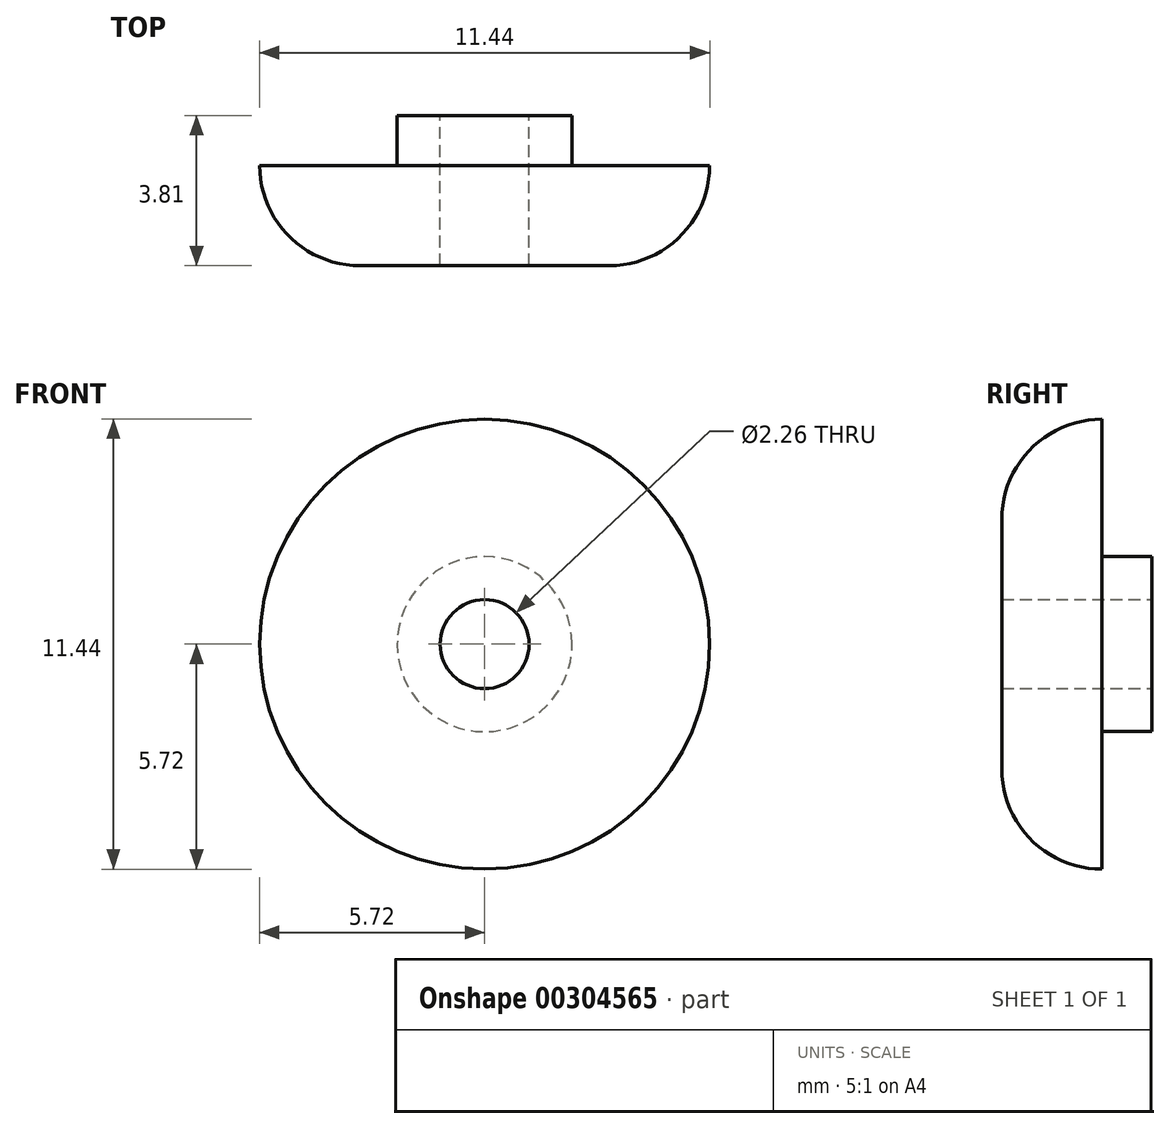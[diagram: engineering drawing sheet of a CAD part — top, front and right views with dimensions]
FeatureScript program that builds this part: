
annotation { "Feature Type Name" : "Feature", "Feature Type Description" : "" }
export const myFeature = defineFeature(function(context is Context, id is Id, definition is map)
    precondition{}
    {
        {
            var Q0;
            Q0=qCreatedBy(makeId("Front.planeOp"),FACE);
            var sketch = newSketch(context, id + "F0", { "sketchPlane" : qUnion([Q0])});
            skCircle(sketch, "E0", {"center": v(0, 0) * mm, "radius": 1.13 * mm});
            skCircle(sketch, "E1", {"center": v(0, 0) * mm, "radius": 2.22 * mm});
            skSolve(sketch);
        }
        {
            var Q0;
            Q0=makeQuery(id+"F0.imprint","IMPRINT",FACE,{"disambiguationData":[TD([[makeQuery(id+"F0.imprint","IMPRINT",EDGE,{"derivedFrom":sQuery(id+"F0.wireOp",EDGE,"E0")}),-1.0]])]});
            extrude(context, id + "F1", {"entities" : qUnion([Q0]), "depth" : 1.27 * mm});
        }
        {
            var Q0;
            Q0=makeQuery(id+"F1.opExtrude","CAP_FACE",FACE,{"disambiguationData":[OSD([sQuery(id+"F0.wireOp",EDGE,"E0"),sQuery(id+"F0.wireOp",EDGE,"E1")])],"isStart":false});
            var sketch = newSketch(context, id + "F2", { "sketchPlane" : qUnion([Q0])});
            skCircle(sketch, "E2", {"center": v(0, 0) * mm, "radius": 5.72 * mm});
            skSolve(sketch);
        }
        {
            var Q0;
            Q0=makeQuery(id+"F2.imprint","IMPRINT",FACE,{"disambiguationData":[TD([[makeQuery(id+"F2.imprint","IMPRINT",EDGE,{"derivedFrom":sQuery(id+"F2.wireOp",EDGE,"E2")}),1.0]])]});
            var Q1;
            Q1=makeQuery(id+"F2.imprint","IMPRINT",FACE,{"disambiguationData":[TD([[makeQuery(id+"F2.imprint","IMPRINT",EDGE,{"derivedFrom":makeQuery(id+"F1.opExtrude","CAP_EDGE",EDGE,{"disambiguationData":[OSD([sQuery(id+"F0.wireOp",EDGE,"E0")])],"isStart":false})}),-1.0]])]});
            var Q2;
            Q2=makeQuery(id+"F2.imprint","IMPRINT",FACE,{"disambiguationData":[TD([[makeQuery(id+"F2.imprint","IMPRINT",EDGE,{"derivedFrom":makeQuery(id+"F1.opExtrude","CAP_EDGE",EDGE,{"disambiguationData":[OSD([sQuery(id+"F0.wireOp",EDGE,"E0")])],"isStart":false})}),1.0]])]});
            extrude(context, id + "F3", {"entities" : qUnion([Q0, Q1, Q2]), "operationType" : NewBodyOperationType.ADD, "depth" : 2.54 * mm});
        }
        {
            var Q0;
            Q0=makeQuery(id+"F3.opExtrude","CAP_EDGE",EDGE,{"disambiguationData":[OSD([sQuery(id+"F2.wireOp",EDGE,"E2")])],"isStart":false});
            fillet(context, id + "F4", {"entities" : qUnion([Q0]), "radius" : 2.54 * mm, "tangentPropagation" : true, "allowEdgeOverflow" : false});
        }
        {
            var Q0;
            Q0=makeQuery(id+"F1.opExtrude","CAP_FACE",FACE,{"disambiguationData":[OSD([sQuery(id+"F0.wireOp",EDGE,"E0"),sQuery(id+"F0.wireOp",EDGE,"E1")])],"isStart":true});
            var sketch = newSketch(context, id + "F5", { "sketchPlane" : qUnion([Q0])});
            skCircle(sketch, "E3", {"center": v(0, 0) * mm, "radius": 1.13 * mm});
            skSolve(sketch);
        }
        {
            var Q0;
            Q0=makeQuery(id+"F5.imprint","IMPRINT",FACE,{"disambiguationData":[TD([[makeQuery(id+"F5.imprint","IMPRINT",EDGE,{"derivedFrom":sQuery(id+"F5.wireOp",EDGE,"E3")}),-1.0]])]});
            extrude(context, id + "F6", {"entities" : qUnion([Q0]), "operationType" : NewBodyOperationType.REMOVE, "oppositeDirection" : true, "depth" : 25.4 * mm});
        }
    });
